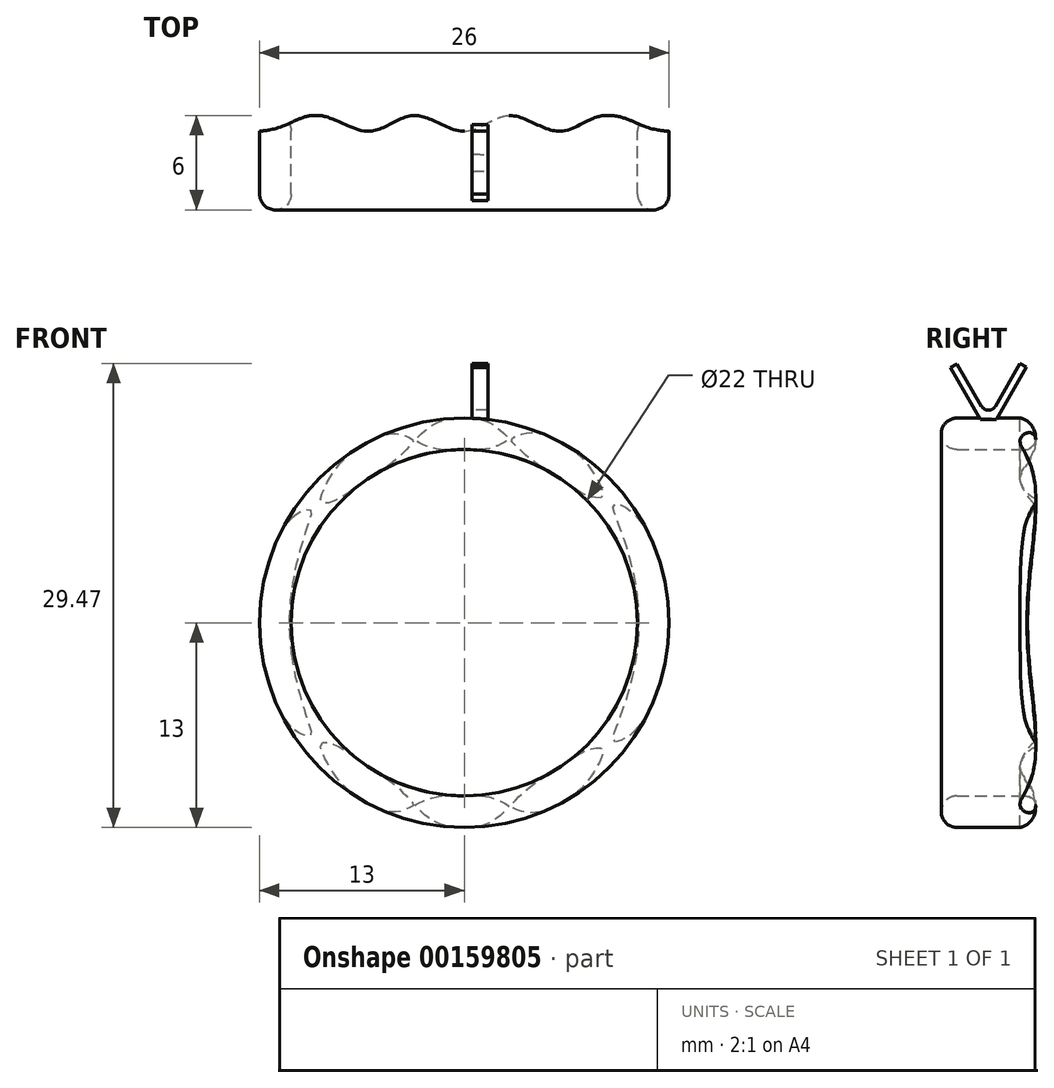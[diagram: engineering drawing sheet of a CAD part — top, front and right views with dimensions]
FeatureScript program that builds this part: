
annotation { "Feature Type Name" : "Feature", "Feature Type Description" : "" }
export const myFeature = defineFeature(function(context is Context, id is Id, definition is map)
    precondition{}
    {
        {
            var Q0;
            Q0=qCreatedBy(makeId("Top.planeOp"),FACE);
            var sketch = newSketch(context, id + "F0", { "sketchPlane" : qUnion([Q0])});
            skLineSegment(sketch, "E0", {"start": v(0, 34.5) * mm, "end": v(0, -43.46) * mm, "construction": true});
            skArc(sketch, "E1", {"start": v(13, 2) * mm, "mid": v(12, 3) * mm, "end": v(11, 2) * mm});
            skArc(sketch, "E2", {"start": v(11, -2) * mm, "mid": v(12, -3) * mm, "end": v(13, -2) * mm});
            skLineSegment(sketch, "E3", {"start": v(11, -2) * mm, "end": v(11, 2) * mm});
            skLineSegment(sketch, "E4", {"start": v(13, -2) * mm, "end": v(13, 2) * mm});
            skSolve(sketch);
        }
        {
            var Q0;
            Q0=makeQuery(id+"F0.imprint","IMPRINT",FACE,{"disambiguationData":[TD([[makeQuery(id+"F0.imprint","IMPRINT",EDGE,{"derivedFrom":sQuery(id+"F0.wireOp",EDGE,"E1")}),1.0]])]});
            var Q1;
            Q1=sQuery(id+"F0.wireOp",EDGE,"E0");
            revolve(context, id + "F1", {"entities" : qUnion([Q0]), "axis" : qUnion([Q1]), "revolveType" : RevolveType.FULL});
        }
        {
            var Q0;
            Q0=qCreatedBy(makeId("Top.planeOp"),FACE);
            var sketch = newSketch(context, id + "F2", { "sketchPlane" : qUnion([Q0])});
            skLineSegment(sketch, "E5.0", {"start": v(-13, -2) * mm, "end": v(13, -2) * mm});
            skLineSegment(sketch, "E6", {"start": v(-12, -3) * mm, "end": v(12, -3) * mm});
            skLineSegment(sketch, "E7", {"start": v(-12, 3) * mm, "end": v(12, 3) * mm});
            skFitSpline(sketch, "E8", {"points": [v(-12, 2) * mm, v(-9.15, 3) * mm, v(-6, 2) * mm, v(-3.15, 3) * mm, v(0, 2) * mm, v(2.85, 3) * mm, v(6, 2) * mm, v(8.85, 3) * mm, v(12, 2) * mm], "startDerivative": vector(24.67, 13.55) * mm, "endDerivative": vector(21.18, -10.47) * mm});
            skLineSegment(sketch, "E9", {"start": v(13.17, 2) * mm, "end": v(13.55, 2) * mm});
            skLineSegment(sketch, "E10", {"start": v(13.55, 2) * mm, "end": v(13.55, 3) * mm});
            skLineSegment(sketch, "E11", {"start": v(13.55, 3) * mm, "end": v(12, 3) * mm});
            skLineSegment(sketch, "E12", {"start": v(-12, 3) * mm, "end": v(-13.86, 3) * mm});
            skLineSegment(sketch, "E13", {"start": v(-13.86, 3) * mm, "end": v(-13.86, 2) * mm});
            skLineSegment(sketch, "E14", {"start": v(-13.86, 2) * mm, "end": v(-13.28, 2) * mm});
            skArc(sketch, "E15.filletArc", {"start": v(-13.28, 2) * mm, "mid": v(-12.1, 2.14) * mm, "end": v(-11, 2.55) * mm});
            skArc(sketch, "E16.filletArc", {"start": v(11.04, 2.47) * mm, "mid": v(12.08, 2.12) * mm, "end": v(13.17, 2) * mm});
            skSolve(sketch);
        }
        {
            var Q0;
            Q0 = qSketchRegion(id + "F2", true);
            extrude(context, id + "F3", {"entities" : qUnion([Q0]), "operationType" : NewBodyOperationType.REMOVE, "endBound" : BoundingType.SYMMETRIC, "depth" : 50 * mm});
        }
        {
            var Q0;
            Q0=qCreatedBy(makeId("Right.planeOp"),FACE);
            cPlane(context, id + "F4", {"entities" : qUnion([Q0]), "cplaneType" : CPlaneType.OFFSET, "offset" : 1 * mm, "width" : 150 * mm, "height" : 150 * mm});
        }
        {
            var Q0;
            Q0=qCreatedBy(id+"F4.planeOp",FACE);
            var sketch = newSketch(context, id + "F5", { "sketchPlane" : qUnion([Q0])});
            skPoint(sketch, "E17.endSnap0", {"position": v(0, 13) * mm});
            skLineSegment(sketch, "E18", {"start": v(-0.43, 13.75) * mm, "end": v(-2, 16.45) * mm});
            skLineSegment(sketch, "E19", {"start": v(-2, 16.45) * mm, "end": v(-2.4, 16.2) * mm});
            skLineSegment(sketch, "E20", {"start": v(-2.4, 16.2) * mm, "end": v(-0.56, 13) * mm});
            skLineSegment(sketch, "E21", {"start": v(0.43, 13.75) * mm, "end": v(2, 16.47) * mm});
            skLineSegment(sketch, "E22", {"start": v(2, 16.47) * mm, "end": v(2.42, 16.23) * mm});
            skLineSegment(sketch, "E23", {"start": v(2.42, 16.23) * mm, "end": v(0.56, 13) * mm});
            skArc(sketch, "E24.filletArc", {"start": v(-0.43, 13.75) * mm, "mid": v(0, 13.5) * mm, "end": v(0.43, 13.75) * mm});
            skPoint(sketch, "E25.orphan", {"position": v(2, 13) * mm});
            skPoint(sketch, "E26.orphan", {"position": v(-2, 13) * mm});
            skLineSegment(sketch, "E27", {"start": v(0.56, 13) * mm, "end": v(0.43, 12.79) * mm});
            skLineSegment(sketch, "E28", {"start": v(-0.56, 13) * mm, "end": v(-0.43, 12.79) * mm});
            skLineSegment(sketch, "E29", {"start": v(0.43, 12.79) * mm, "end": v(-0.43, 12.79) * mm});
            skSolve(sketch);
        }
        {
            var Q0;
            Q0 = qSketchRegion(id + "F5", true);
            extrude(context, id + "F6", {"entities" : qUnion([Q0]), "operationType" : NewBodyOperationType.ADD, "endBound" : BoundingType.SYMMETRIC, "depth" : 1 * mm});
        }
    });
